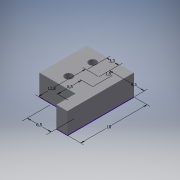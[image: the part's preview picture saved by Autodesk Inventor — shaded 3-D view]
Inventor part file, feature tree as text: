
AUTODESK INVENTOR PART (.ipt)
format: ipt  version: 2016 (Build 200138000, 138)  size: 107,008 bytes
history: native  units: mm
features: sketch x1, extrude x1, hole x1
ambient origin geometry x8: Origin, YZ Plane, XZ Plane, XY Plane, X Axis, Y Axis, Z Axis, Center Point
bodies: Solid1 (feature_tree)
feature tree (3):
  sketch  "Sketch1"  dims[d0=6.5mm d5=12.8mm d6=18.0mm d7=9.5mm d8=3.3mm d9=5.7mm d10=0.0mm d13=6.5mm d14=1.5mm d15=2.1mm d16=6.0mm d17=4.0mm d18=2.0mm d19=90.0deg d20=8.0mm d21=20.594885mm]
  extrude  "Extrusion1"  Depth=12.8mm
  hole  "Hole1"  [1 undecoded]
note: 1 required parameter value undecoded (feature->parameter linkage not recoverable at this tier; creation-order binding heuristic only, values carry confidence <= 0.55)
